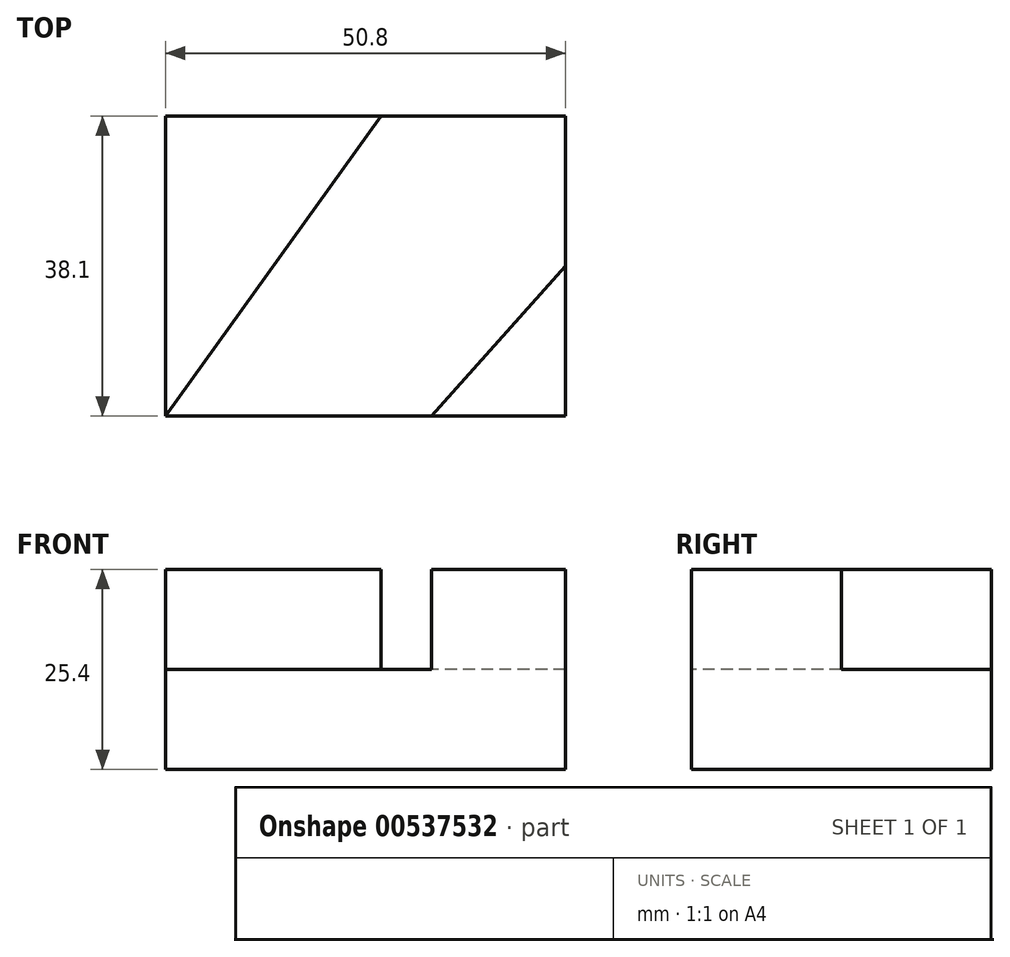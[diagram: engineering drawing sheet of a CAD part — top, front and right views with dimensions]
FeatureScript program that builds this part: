
annotation { "Feature Type Name" : "Feature", "Feature Type Description" : "" }
export const myFeature = defineFeature(function(context is Context, id is Id, definition is map)
    precondition{}
    {
        {
            var Q0;
            Q0=qCreatedBy(makeId("Front.planeOp"),FACE);
            var sketch = newSketch(context, id + "F0", { "sketchPlane" : qUnion([Q0])});
            skLineSegment(sketch, "E0", {"start": v(0, 0) * mm, "end": v(50.8, 0) * mm});
            skLineSegment(sketch, "E1", {"start": v(50.8, 0) * mm, "end": v(50.8, 12.7) * mm});
            skLineSegment(sketch, "E2", {"start": v(50.8, 12.7) * mm, "end": v(0, 12.7) * mm});
            skLineSegment(sketch, "E3", {"start": v(0, 12.7) * mm, "end": v(0, 0) * mm});
            skSolve(sketch);
        }
        {
            var Q0;
            Q0=makeQuery(id+"F0.imprint","IMPRINT",FACE,{"disambiguationData":[TD([[makeQuery(id+"F0.imprint","IMPRINT",EDGE,{"derivedFrom":sQuery(id+"F0.wireOp",EDGE,"E0")}),1.0]])]});
            extrude(context, id + "F1", {"entities" : qUnion([Q0]), "depth" : 38.1 * mm, "offsetDistance" : 25.4 * mm});
        }
        {
            var Q0;
            Q0=makeQuery(id+"F1.opExtrude","SWEPT_FACE",FACE,{"disambiguationData":[OSD([sQuery(id+"F0.wireOp",EDGE,"E2")])]});
            var sketch = newSketch(context, id + "F2", { "sketchPlane" : qUnion([Q0])});
            skLineSegment(sketch, "E4", {"start": v(27.35, 0) * mm, "end": v(0, -38.1) * mm});
            skLineSegment(sketch, "E5", {"start": v(50.8, -19.05) * mm, "end": v(33.76, -38.1) * mm});
            skSolve(sketch);
        }
        {
            var Q0;
            {var subQ0=sQuery(id+"F2.wireOp",EDGE,"E4");Q0=makeQuery(id+"F2.imprint","IMPRINT",FACE,{"disambiguationData":[TD([[makeQuery(id+"F2.imprint","IMPRINT",EDGE,{"derivedFrom":subQ0}),-1.0]])]});}
            var Q1;
            {var subQ0=sQuery(id+"F2.wireOp",EDGE,"E5");Q1=makeQuery(id+"F2.imprint","IMPRINT",FACE,{"disambiguationData":[TD([[makeQuery(id+"F2.imprint","IMPRINT",EDGE,{"derivedFrom":subQ0}),1.0]])]});}
            extrude(context, id + "F3", {"entities" : qUnion([Q0, Q1]), "operationType" : NewBodyOperationType.ADD, "depth" : 12.7 * mm, "offsetDistance" : 25.4 * mm});
        }
    });
